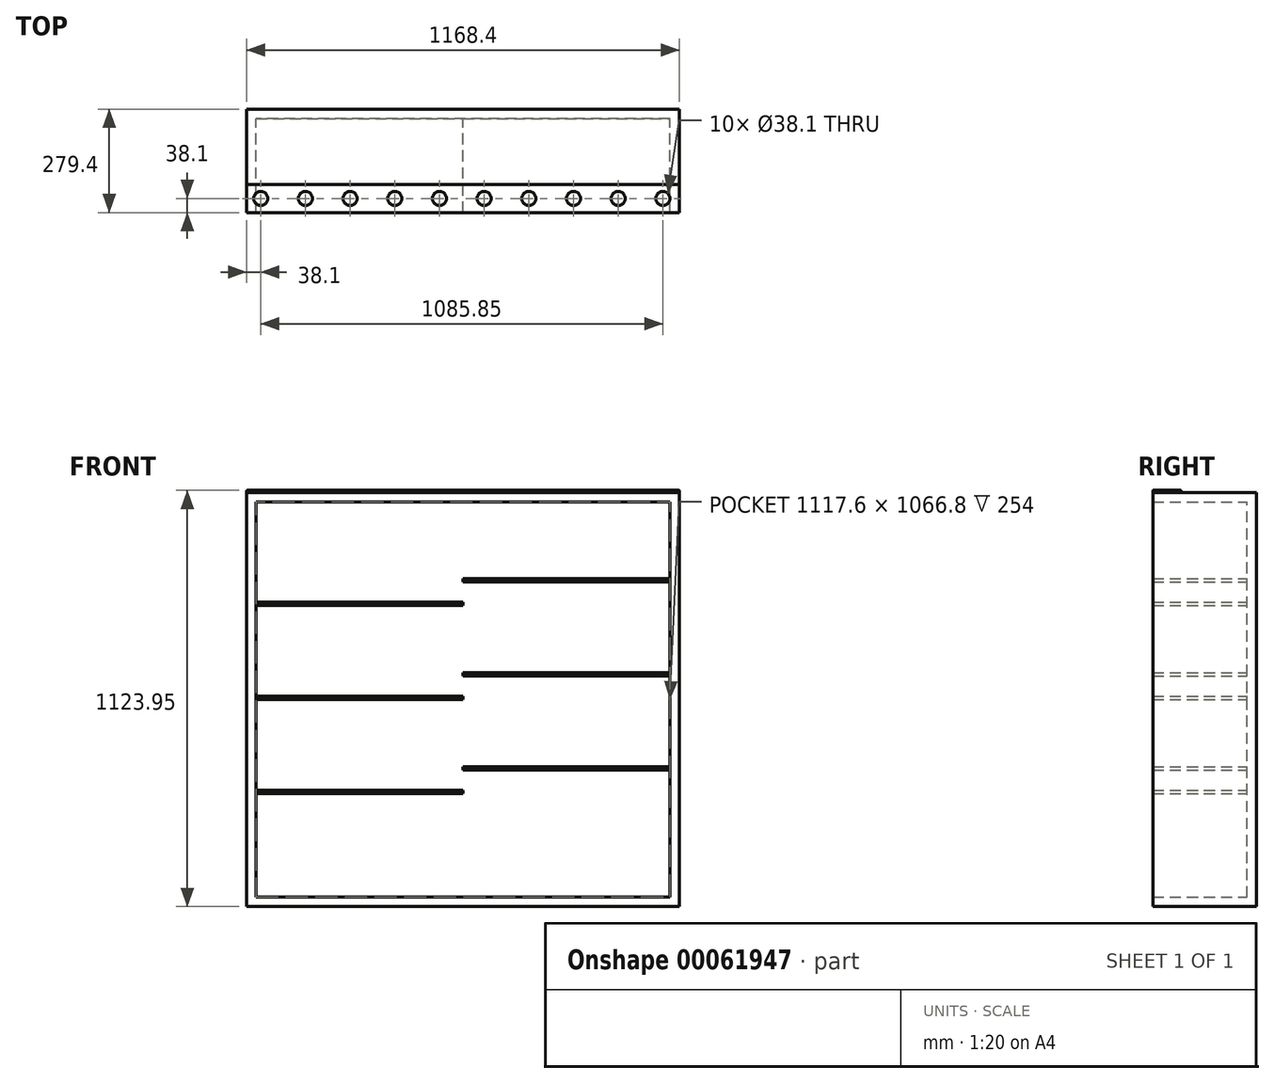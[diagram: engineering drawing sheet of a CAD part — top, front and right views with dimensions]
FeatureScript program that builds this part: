
annotation { "Feature Type Name" : "Feature", "Feature Type Description" : "" }
export const myFeature = defineFeature(function(context is Context, id is Id, definition is map)
    precondition{}
    {
        {
            var Q0;
            Q0=qCreatedBy(makeId("Front.planeOp"),FACE);
            var sketch = newSketch(context, id + "F0", { "sketchPlane" : qUnion([Q0])});
            skLineSegment(sketch, "E0.rect.bottom", {"start": v(584.2, -558.8) * mm, "end": v(-584.2, -558.8) * mm});
            skLineSegment(sketch, "E0.rect.top", {"start": v(584.2, 558.8) * mm, "end": v(-584.2, 558.8) * mm});
            skLineSegment(sketch, "E0.rect.left", {"start": v(584.2, -558.8) * mm, "end": v(584.2, 558.8) * mm});
            skLineSegment(sketch, "E0.rect.right", {"start": v(-584.2, -558.8) * mm, "end": v(-584.2, 558.8) * mm});
            skPoint(sketch, "E0.rect.middle", {"position": v(0, 0) * mm});
            skSolve(sketch);
        }
        {
            var Q0;
            Q0=makeQuery(id+"F0.imprint","IMPRINT",FACE,{"disambiguationData":[TD([[makeQuery(id+"F0.imprint","IMPRINT",EDGE,{"derivedFrom":sQuery(id+"F0.wireOp",EDGE,"E0.rect.bottom")}),-1.0]])]});
            extrude(context, id + "F1", {"entities" : qUnion([Q0]), "depth" : 279.4 * mm});
        }
        {
            var Q0;
            Q0=makeQuery(id+"F1.opExtrude","CAP_FACE",FACE,{"disambiguationData":[OSD([sQuery(id+"F0.wireOp",EDGE,"E0.rect.bottom"),sQuery(id+"F0.wireOp",EDGE,"E0.rect.top"),sQuery(id+"F0.wireOp",EDGE,"E0.rect.left"),sQuery(id+"F0.wireOp",EDGE,"E0.rect.right")])],"isStart":false});
            shell(context, id + "F2", {"entities" : qUnion([Q0]), "thickness" : 25.4 * mm});
        }
        {
            var Q0;
            Q0=makeQuery(id+"F2.opShell","OFFSET_FACE",FACE,{"disambiguationData":[OSD([sQuery(id+"F0.wireOp",EDGE,"E0.rect.bottom"),sQuery(id+"F0.wireOp",EDGE,"E0.rect.top"),sQuery(id+"F0.wireOp",EDGE,"E0.rect.left"),sQuery(id+"F0.wireOp",EDGE,"E0.rect.right")])]});
            var sketch = newSketch(context, id + "F3", { "sketchPlane" : qUnion([Q0])});
            skLineSegment(sketch, "E1.0.1.0", {"start": v(25.4, 9.12) * mm, "end": v(25.4, 9.12) * mm});
            skLineSegment(sketch, "E1.6.1.0", {"start": v(25.4, -0.4) * mm, "end": v(25.4, 0) * mm});
            skLineSegment(sketch, "E2.1.0.1", {"start": v(584.2, 0) * mm, "end": v(584.2, 0) * mm});
            skLineSegment(sketch, "E3.trimOffspring", {"start": v(25.4, 0) * mm, "end": v(25.4, 0) * mm, "construction": true});
            skPoint(sketch, "E4.trimOffspring.end.orphan", {"position": v(0, -533.4) * mm});
            skPoint(sketch, "E5.start.orphan", {"position": v(0, 533.4) * mm});
            skLineSegment(sketch, "E6", {"start": v(0, 0) * mm, "end": v(-558.8, 0) * mm, "construction": true});
            skLineSegment(sketch, "E7", {"start": v(0, 63.5) * mm, "end": v(558.8, 63.5) * mm, "construction": true});
            skLineSegment(sketch, "E8.bottom", {"start": v(-558.8, 0) * mm, "end": v(0, 0) * mm});
            skLineSegment(sketch, "E8.top", {"start": v(-558.8, 9.53) * mm, "end": v(0, 9.53) * mm});
            skLineSegment(sketch, "E8.left", {"start": v(-558.8, 0) * mm, "end": v(-558.8, 9.53) * mm});
            skLineSegment(sketch, "E8.right", {"start": v(0, 0) * mm, "end": v(0, 9.53) * mm});
            skLineSegment(sketch, "E9.bottom", {"start": v(0, 63.5) * mm, "end": v(558.8, 63.5) * mm});
            skLineSegment(sketch, "E9.top", {"start": v(0, 73.02) * mm, "end": v(558.8, 73.02) * mm});
            skLineSegment(sketch, "E9.left", {"start": v(0, 63.5) * mm, "end": v(0, 73.02) * mm});
            skLineSegment(sketch, "E9.right", {"start": v(558.8, 63.5) * mm, "end": v(558.8, 73.02) * mm});
            skSolve(sketch);
        }
        {
            var Q0;
            Q0=makeQuery(id+"F3.imprint","IMPRINT",FACE,{"disambiguationData":[TD([[makeQuery(id+"F3.imprint","IMPRINT",EDGE,{"derivedFrom":sQuery(id+"F3.wireOp",EDGE,"E8.bottom")}),1.0]])]});
            var Q1;
            Q1=makeQuery(id+"F3.imprint","IMPRINT",FACE,{"disambiguationData":[TD([[makeQuery(id+"F3.imprint","IMPRINT",EDGE,{"derivedFrom":sQuery(id+"F3.wireOp",EDGE,"E9.bottom")}),1.0]])]});
            extrude(context, id + "F4", {"entities" : qUnion([Q0, Q1]), "depth" : 254 * mm});
        }
        {
            var Q0;
            Q0=makeQuery(id+"F4.opExtrude","SWEPT_BODY",BODY,{"disambiguationData":[OSD([sQuery(id+"F3.wireOp",EDGE,"E8.bottom"),sQuery(id+"F3.wireOp",EDGE,"E8.top"),sQuery(id+"F3.wireOp",EDGE,"E8.left"),sQuery(id+"F3.wireOp",EDGE,"E8.right")])]});
            var Q1;
            Q1=makeQuery(id+"F4.opExtrude","SWEPT_BODY",BODY,{"disambiguationData":[OSD([sQuery(id+"F3.wireOp",EDGE,"E9.bottom"),sQuery(id+"F3.wireOp",EDGE,"E9.top"),sQuery(id+"F3.wireOp",EDGE,"E9.left"),sQuery(id+"F3.wireOp",EDGE,"E9.right")])]});
            transform(context, id + "F5", {"entities" : qUnion([Q0, Q1]), "transformType" : TransformType.COPY});
        }
        {
            var Q0;
            Q0=makeQuery(id+"F4.opExtrude","SWEPT_BODY",BODY,{"disambiguationData":[OSD([sQuery(id+"F3.wireOp",EDGE,"E8.bottom"),sQuery(id+"F3.wireOp",EDGE,"E8.top"),sQuery(id+"F3.wireOp",EDGE,"E8.left"),sQuery(id+"F3.wireOp",EDGE,"E8.right")])]});
            var Q1;
            Q1=makeQuery(id+"F4.opExtrude","SWEPT_BODY",BODY,{"disambiguationData":[OSD([sQuery(id+"F3.wireOp",EDGE,"E9.bottom"),sQuery(id+"F3.wireOp",EDGE,"E9.top"),sQuery(id+"F3.wireOp",EDGE,"E9.left"),sQuery(id+"F3.wireOp",EDGE,"E9.right")])]});
            transform(context, id + "F6", {"entities" : qUnion([Q0, Q1]), "transformType" : TransformType.TRANSLATION_3D, "dx" : 0 * mm, "dy" : 0 * mm, "dz" : 254 * mm, "makeCopy" : false});
        }
        {
            var Q0;
            Q0=makeQuery(id+"F5.opPattern","COPY",BODY,{"derivedFrom":makeQuery(id+"F4.opExtrude","SWEPT_BODY",BODY,{"disambiguationData":[OSD([sQuery(id+"F3.wireOp",EDGE,"E8.bottom"),sQuery(id+"F3.wireOp",EDGE,"E8.top"),sQuery(id+"F3.wireOp",EDGE,"E8.left"),sQuery(id+"F3.wireOp",EDGE,"E8.right")])]}),"instanceName":"1"});
            var Q1;
            Q1=makeQuery(id+"F5.opPattern","COPY",BODY,{"derivedFrom":makeQuery(id+"F4.opExtrude","SWEPT_BODY",BODY,{"disambiguationData":[OSD([sQuery(id+"F3.wireOp",EDGE,"E9.bottom"),sQuery(id+"F3.wireOp",EDGE,"E9.top"),sQuery(id+"F3.wireOp",EDGE,"E9.left"),sQuery(id+"F3.wireOp",EDGE,"E9.right")])]}),"instanceName":"1"});
            transform(context, id + "F7", {"entities" : qUnion([Q0, Q1]), "transformType" : TransformType.COPY});
        }
        {
            var Q0;
            Q0=makeQuery(id+"F5.opPattern","COPY",BODY,{"derivedFrom":makeQuery(id+"F4.opExtrude","SWEPT_BODY",BODY,{"disambiguationData":[OSD([sQuery(id+"F3.wireOp",EDGE,"E8.bottom"),sQuery(id+"F3.wireOp",EDGE,"E8.top"),sQuery(id+"F3.wireOp",EDGE,"E8.left"),sQuery(id+"F3.wireOp",EDGE,"E8.right")])]}),"instanceName":"1"});
            var Q1;
            Q1=makeQuery(id+"F5.opPattern","COPY",BODY,{"derivedFrom":makeQuery(id+"F4.opExtrude","SWEPT_BODY",BODY,{"disambiguationData":[OSD([sQuery(id+"F3.wireOp",EDGE,"E9.bottom"),sQuery(id+"F3.wireOp",EDGE,"E9.top"),sQuery(id+"F3.wireOp",EDGE,"E9.left"),sQuery(id+"F3.wireOp",EDGE,"E9.right")])]}),"instanceName":"1"});
            transform(context, id + "F8", {"entities" : qUnion([Q0, Q1]), "transformType" : TransformType.TRANSLATION_3D, "dx" : 0 * mm, "dy" : 0 * mm, "dz" : -254 * mm, "makeCopy" : false});
        }
        {
            var Q0;
            Q0=makeQuery(id+"F1.opExtrude","SWEPT_FACE",FACE,{"disambiguationData":[OSD([sQuery(id+"F0.wireOp",EDGE,"E0.rect.top")])]});
            var sketch = newSketch(context, id + "F9", { "sketchPlane" : qUnion([Q0])});
            skLineSegment(sketch, "E10.bottom", {"start": v(-584.2, -279.4) * mm, "end": v(584.2, -279.4) * mm});
            skLineSegment(sketch, "E10.top", {"start": v(-584.2, -203.2) * mm, "end": v(584.2, -203.2) * mm});
            skLineSegment(sketch, "E10.left", {"start": v(-584.2, -279.4) * mm, "end": v(-584.2, -203.2) * mm});
            skLineSegment(sketch, "E10.right", {"start": v(584.2, -279.4) * mm, "end": v(584.2, -203.2) * mm});
            skSolve(sketch);
        }
        {
            var Q0;
            Q0=makeQuery(id+"F9.imprint","IMPRINT",FACE,{"disambiguationData":[TD([[makeQuery(id+"F9.imprint","IMPRINT",EDGE,{"derivedFrom":sQuery(id+"F9.wireOp",EDGE,"E10.bottom")}),-1.0]])]});
            extrude(context, id + "F10", {"entities" : qUnion([Q0]), "depth" : 6.35 * mm});
        }
        {
            var Q0;
            Q0=makeQuery(id+"F10.opExtrude","CAP_FACE",FACE,{"disambiguationData":[OSD([sQuery(id+"F9.wireOp",EDGE,"E10.bottom"),sQuery(id+"F9.wireOp",EDGE,"E10.top"),sQuery(id+"F9.wireOp",EDGE,"E10.left"),sQuery(id+"F9.wireOp",EDGE,"E10.right")])],"isStart":false});
            var sketch = newSketch(context, id + "F11", { "sketchPlane" : qUnion([Q0])});
            skLineSegment(sketch, "E11", {"start": v(-584.2, -241.3) * mm, "end": v(-546.1, -241.3) * mm, "construction": true});
            skCircle(sketch, "E12", {"center": v(-546.1, -241.3) * mm, "radius": 19.05 * mm});
            skCircle(sketch, "E13.1.0.0", {"center": v(-425.45, -241.3) * mm, "radius": 19.05 * mm});
            skCircle(sketch, "E13.2.0.0", {"center": v(-304.8, -241.3) * mm, "radius": 19.05 * mm});
            skCircle(sketch, "E13.3.0.0", {"center": v(-184.15, -241.3) * mm, "radius": 19.05 * mm});
            skCircle(sketch, "E13.4.0.0", {"center": v(-63.5, -241.3) * mm, "radius": 19.05 * mm});
            skCircle(sketch, "E13.5.0.0", {"center": v(57.15, -241.3) * mm, "radius": 19.05 * mm});
            skCircle(sketch, "E13.6.0.0", {"center": v(177.8, -241.3) * mm, "radius": 19.05 * mm});
            skCircle(sketch, "E13.7.0.0", {"center": v(298.45, -241.3) * mm, "radius": 19.05 * mm});
            skCircle(sketch, "E13.8.0.0", {"center": v(419.1, -241.3) * mm, "radius": 19.05 * mm});
            skCircle(sketch, "E13.9.0.0", {"center": v(539.75, -241.3) * mm, "radius": 19.05 * mm});
            skLineSegment(sketch, "E13.direction1", {"start": v(-546.1, -241.3) * mm, "end": v(-425.45, -241.3) * mm, "construction": true});
            skSolve(sketch);
        }
        {
            var Q0;
            Q0=makeQuery(id+"F11.imprint","IMPRINT",FACE,{"disambiguationData":[TD([[makeQuery(id+"F11.imprint","IMPRINT",EDGE,{"derivedFrom":sQuery(id+"F11.wireOp",EDGE,"E12")}),1.0]])]});
            var Q1;
            Q1=makeQuery(id+"F11.imprint","IMPRINT",FACE,{"disambiguationData":[TD([[makeQuery(id+"F11.imprint","IMPRINT",EDGE,{"derivedFrom":sQuery(id+"F11.wireOp",EDGE,"E13.1.0.0")}),1.0]])]});
            var Q2;
            Q2=makeQuery(id+"F11.imprint","IMPRINT",FACE,{"disambiguationData":[TD([[makeQuery(id+"F11.imprint","IMPRINT",EDGE,{"derivedFrom":sQuery(id+"F11.wireOp",EDGE,"E13.2.0.0")}),1.0]])]});
            var Q3;
            Q3=makeQuery(id+"F11.imprint","IMPRINT",FACE,{"disambiguationData":[TD([[makeQuery(id+"F11.imprint","IMPRINT",EDGE,{"derivedFrom":sQuery(id+"F11.wireOp",EDGE,"E13.3.0.0")}),1.0]])]});
            var Q4;
            Q4=makeQuery(id+"F11.imprint","IMPRINT",FACE,{"disambiguationData":[TD([[makeQuery(id+"F11.imprint","IMPRINT",EDGE,{"derivedFrom":sQuery(id+"F11.wireOp",EDGE,"E13.4.0.0")}),1.0]])]});
            var Q5;
            Q5=makeQuery(id+"F11.imprint","IMPRINT",FACE,{"disambiguationData":[TD([[makeQuery(id+"F11.imprint","IMPRINT",EDGE,{"derivedFrom":sQuery(id+"F11.wireOp",EDGE,"E13.5.0.0")}),1.0]])]});
            var Q6;
            Q6=makeQuery(id+"F11.imprint","IMPRINT",FACE,{"disambiguationData":[TD([[makeQuery(id+"F11.imprint","IMPRINT",EDGE,{"derivedFrom":sQuery(id+"F11.wireOp",EDGE,"E13.6.0.0")}),1.0]])]});
            var Q7;
            Q7=makeQuery(id+"F11.imprint","IMPRINT",FACE,{"disambiguationData":[TD([[makeQuery(id+"F11.imprint","IMPRINT",EDGE,{"derivedFrom":sQuery(id+"F11.wireOp",EDGE,"E13.7.0.0")}),1.0]])]});
            var Q8;
            Q8=makeQuery(id+"F11.imprint","IMPRINT",FACE,{"disambiguationData":[TD([[makeQuery(id+"F11.imprint","IMPRINT",EDGE,{"derivedFrom":sQuery(id+"F11.wireOp",EDGE,"E13.8.0.0")}),1.0]])]});
            var Q9;
            Q9=makeQuery(id+"F11.imprint","IMPRINT",FACE,{"disambiguationData":[TD([[makeQuery(id+"F11.imprint","IMPRINT",EDGE,{"derivedFrom":sQuery(id+"F11.wireOp",EDGE,"E13.9.0.0")}),1.0]])]});
            var Q10;
            Q10=makeQuery(id+"F1.opExtrude","SWEPT_FACE",FACE,{"disambiguationData":[OSD([sQuery(id+"F0.wireOp",EDGE,"E0.rect.top")])]});
            var Q11;
            Q11=makeQuery(id+"F1.opExtrude","SWEPT_BODY",BODY,{"disambiguationData":[OSD([sQuery(id+"F0.wireOp",EDGE,"E0.rect.bottom"),sQuery(id+"F0.wireOp",EDGE,"E0.rect.top"),sQuery(id+"F0.wireOp",EDGE,"E0.rect.left"),sQuery(id+"F0.wireOp",EDGE,"E0.rect.right")])]});
            extrude(context, id + "F12", {"entities" : qUnion([Q0, Q1, Q2, Q3, Q4, Q5, Q6, Q7, Q8, Q9]), "operationType" : NewBodyOperationType.REMOVE, "endBound" : BoundingType.UP_TO_SURFACE, "oppositeDirection" : true, "endBoundEntityFace" : qUnion([Q10]), "endBoundEntityBody" : qUnion([Q11]), "depth" : 25.4 * mm});
        }
        {
            var Q0;
            Q0=makeQuery(id+"F12.boolean.opBoolean","COPY",EDGE,{"derivedFrom":makeQuery(id+"F12.opExtrude","CAP_EDGE",EDGE,{"disambiguationData":[OSD([sQuery(id+"F11.wireOp",EDGE,"E12")])],"isStart":true})});
            var Q1;
            Q1=makeQuery(id+"F12.boolean.opBoolean","COPY",EDGE,{"derivedFrom":makeQuery(id+"F12.opExtrude","CAP_EDGE",EDGE,{"disambiguationData":[OSD([sQuery(id+"F11.wireOp",EDGE,"E13.1.0.0")])],"isStart":true})});
            var Q2;
            Q2=makeQuery(id+"F10.opExtrude","CAP_EDGE",EDGE,{"disambiguationData":[OSD([sQuery(id+"F9.wireOp",EDGE,"E10.top")])],"isStart":false});
            var Q3;
            Q3=makeQuery(id+"F10.opExtrude","CAP_EDGE",EDGE,{"disambiguationData":[OSD([sQuery(id+"F9.wireOp",EDGE,"E10.left")])],"isStart":false});
            var Q4;
            Q4=makeQuery(id+"F10.opExtrude","CAP_EDGE",EDGE,{"disambiguationData":[OSD([sQuery(id+"F9.wireOp",EDGE,"E10.bottom")])],"isStart":false});
            var Q5;
            Q5=makeQuery(id+"F12.boolean.opBoolean","COPY",EDGE,{"derivedFrom":makeQuery(id+"F12.opExtrude","CAP_EDGE",EDGE,{"disambiguationData":[OSD([sQuery(id+"F11.wireOp",EDGE,"E13.2.0.0")])],"isStart":true})});
            var Q6;
            Q6=makeQuery(id+"F12.boolean.opBoolean","COPY",EDGE,{"derivedFrom":makeQuery(id+"F12.opExtrude","CAP_EDGE",EDGE,{"disambiguationData":[OSD([sQuery(id+"F11.wireOp",EDGE,"E13.3.0.0")])],"isStart":true})});
            var Q7;
            Q7=makeQuery(id+"F12.boolean.opBoolean","COPY",EDGE,{"derivedFrom":makeQuery(id+"F12.opExtrude","CAP_EDGE",EDGE,{"disambiguationData":[OSD([sQuery(id+"F11.wireOp",EDGE,"E13.4.0.0")])],"isStart":true})});
            var Q8;
            Q8=makeQuery(id+"F12.boolean.opBoolean","COPY",EDGE,{"derivedFrom":makeQuery(id+"F12.opExtrude","CAP_EDGE",EDGE,{"disambiguationData":[OSD([sQuery(id+"F11.wireOp",EDGE,"E13.5.0.0")])],"isStart":true})});
            var Q9;
            Q9=makeQuery(id+"F12.boolean.opBoolean","COPY",EDGE,{"derivedFrom":makeQuery(id+"F12.opExtrude","CAP_EDGE",EDGE,{"disambiguationData":[OSD([sQuery(id+"F11.wireOp",EDGE,"E13.6.0.0")])],"isStart":true})});
            var Q10;
            Q10=makeQuery(id+"F12.boolean.opBoolean","COPY",EDGE,{"derivedFrom":makeQuery(id+"F12.opExtrude","CAP_EDGE",EDGE,{"disambiguationData":[OSD([sQuery(id+"F11.wireOp",EDGE,"E13.7.0.0")])],"isStart":true})});
            var Q11;
            Q11=makeQuery(id+"F12.boolean.opBoolean","COPY",EDGE,{"derivedFrom":makeQuery(id+"F12.opExtrude","CAP_EDGE",EDGE,{"disambiguationData":[OSD([sQuery(id+"F11.wireOp",EDGE,"E13.8.0.0")])],"isStart":true})});
            var Q12;
            Q12=makeQuery(id+"F12.boolean.opBoolean","COPY",EDGE,{"derivedFrom":makeQuery(id+"F12.opExtrude","CAP_EDGE",EDGE,{"disambiguationData":[OSD([sQuery(id+"F11.wireOp",EDGE,"E13.9.0.0")])],"isStart":true})});
            var Q13;
            Q13=makeQuery(id+"F10.opExtrude","CAP_EDGE",EDGE,{"disambiguationData":[OSD([sQuery(id+"F9.wireOp",EDGE,"E10.right")])],"isStart":false});
            fillet(context, id + "F13", {"entities" : qUnion([Q0, Q1, Q2, Q3, Q4, Q5, Q6, Q7, Q8, Q9, Q10, Q11, Q12, Q13]), "radius" : 1.59 * mm, "tangentPropagation" : true, "allowEdgeOverflow" : false});
        }
    });
